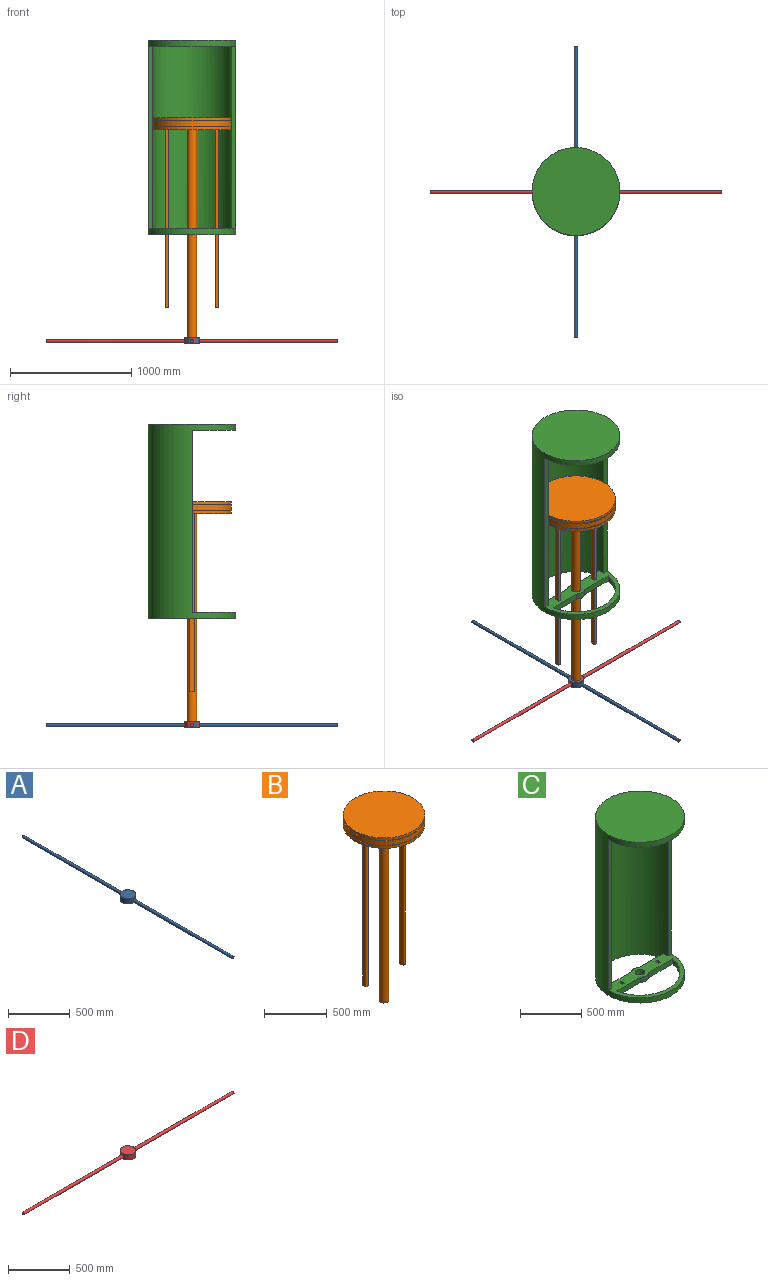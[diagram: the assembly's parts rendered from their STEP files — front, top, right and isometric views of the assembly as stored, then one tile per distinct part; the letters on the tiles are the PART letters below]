
ASSEMBLY  parts=4 mates=3
PART A: 7 faces, bbox 127x2400x50.8 mm
  f0: cylinder r=63.5mm len=127mm, axis (0,0,1), area 19254.8mm2, adj f1,f2,f4,f5
  f1: plane 127x127mm, normal (0,0,-1), area 12667.7mm2, adj f0
  f2: plane 127x127mm, normal (0,0,1), area 12667.7mm2, adj f0
  f3: plane 25.4x25.4mm, normal (0,1,0), area 506.7mm2, adj f4
  f4: cylinder r=12.7mm len=1137.78mm, axis (0,1,0), area 90739.8mm2, adj f0,f3
  f5: cylinder r=12.7mm len=1137.78mm, axis (0,1,0), area 90739.7mm2, adj f0,f6
  f6: plane 25.4x25.4mm, normal (0,-1,0), area 506.7mm2, adj f5
PART B: 25 faces, bbox 648.8x648.8x1813.5 mm
  f0: cylinder r=324.42mm len=648.84mm, axis (0,0,-1), area 48539.4mm2, adj f1,f6
  f1: plane 648.84x648.84mm, normal (0,0,-1), area 142883.7mm2, adj f0,f2
  f2: cylinder r=244.47mm len=488.95mm, axis (0,0,-1), area 58524.7mm2, adj f1,f3
  f3: plane 488.95x488.95mm, normal (0,0,-1), area 181270.9mm2, adj f2,f13,f15,f16,f17,f18,f20,f21
  f4: plane 648.84x648.84mm, normal (0,0,-1), area 6440.3mm2, adj f5,f7
  f5: cylinder r=321.25mm len=642.49mm, axis (0,0,1), area 6408.6mm2, adj f4,f6
  f6: plane 648.84x648.84mm, normal (0,0,1), area 6440.3mm2, adj f0,f5
  f7: cylinder r=324.42mm len=648.84mm, axis (0,0,-1), area 97078.8mm2, adj f4,f10
  f8: plane 648.84x648.84mm, normal (0,0,-1), area 6440.3mm2, adj f9,f12
  f9: cylinder r=321.25mm len=642.49mm, axis (0,0,1), area 6408.6mm2, adj f8,f10
  f10: plane 648.84x648.84mm, normal (0,0,1), area 6440.3mm2, adj f7,f9
  f11: plane 648.84x648.84mm, normal (0,0,1), area 330650.5mm2, adj f12
  f12: cylinder r=324.42mm len=648.84mm, axis (0,0,-1), area 48539.4mm2, adj f8,f11
  f13: cylinder r=38.1mm len=1750mm, axis (0,0,1), area 418931.4mm2, adj f3,f14
  f14: plane 76.2x76.2mm, normal (0,0,-1), area 4560.4mm2, adj f13
  f15: plane 1500x25.4mm, normal (0,-1,0), area 38100mm2, adj f3,f16,f18,f19
  f16: plane 1500x38.1mm, normal (-1,0,0), area 57150mm2, adj f3,f15,f17,f19
  f17: plane 1500x25.4mm, normal (0,1,0), area 38100mm2, adj f3,f16,f18,f19
  f18: plane 1500x38.1mm, normal (1,0,0), area 57150mm2, adj f3,f15,f17,f19
  f19: plane 38.1x25.4mm, normal (0,0,-1), area 967.7mm2, adj f15,f16,f17,f18
  f20: plane 1500x38.1mm, normal (1,0,0), area 57150mm2, adj f3,f21,f23,f24
  f21: plane 1500x25.4mm, normal (0,-1,0), area 38100mm2, adj f3,f20,f22,f24
  f22: plane 1500x38.1mm, normal (-1,0,0), area 57150mm2, adj f3,f21,f23,f24
  f23: plane 1500x25.4mm, normal (0,1,0), area 38100mm2, adj f3,f20,f22,f24
  f24: plane 38.1x25.4mm, normal (0,0,-1), area 967.7mm2, adj f20,f21,f22,f23
PART C: 24 faces, bbox 723.9x723.9x1601.6 mm
  f0: plane 723.9x431.8mm, normal (0,0,1), area 105607.8mm2, adj f1,f2,f3,f4,f5,f6,f7,f8
  f1: plane 275.56x50.8mm, normal (0,-1,0), area 13998.6mm2, adj f0,f2,f18,f19
  f2: cylinder r=69.85mm len=88.67mm, axis (0,0,-1), area 4880.2mm2, adj f0,f1,f3,f19
  f3: plane 275.56x50.8mm, normal (0,-1,0), area 13998.6mm2, adj f0,f2,f18,f19
  f4: cylinder r=324.42mm len=1550.8mm, axis (0,0,-1), area 1575066.2mm2, adj f0,f5,f13,f19,f20,f21,f22
  f5: plane 275.56x50.8mm, normal (0,1,0), area 13998.6mm2, adj f0,f4,f6,f19
  f6: cylinder r=69.85mm len=88.67mm, axis (0,0,-1), area 4880.2mm2, adj f0,f5,f13,f19
  f7: plane 50.8x25.4mm, normal (0,-1,0), area 1290.3mm2, adj f0,f8,f14,f19
  f8: plane 50.8x38.1mm, normal (-1,0,0), area 1935.5mm2, adj f0,f7,f9,f19
  f9: plane 50.8x25.4mm, normal (0,1,0), area 1290.3mm2, adj f0,f8,f14,f19
  f10: plane 50.8x38.1mm, normal (1,0,0), area 1935.5mm2, adj f0,f11,f17,f19
  f11: plane 50.8x25.4mm, normal (0,-1,0), area 1290.3mm2, adj f0,f10,f12,f19
  f12: plane 50.8x38.1mm, normal (-1,0,0), area 1935.5mm2, adj f0,f11,f17,f19
  f13: plane 275.56x50.8mm, normal (0,1,0), area 13998.6mm2, adj f0,f4,f6,f19
  f14: plane 50.8x38.1mm, normal (1,0,0), area 1935.5mm2, adj f0,f7,f9,f19
  f15: cylinder r=361.95mm len=1601.6mm, axis (0,0,-1), area 1936707.8mm2, adj f0,f19,f20,f21,f22,f23
  f16: cylinder r=38.1mm len=76.2mm, axis (0,0,-1), area 12161mm2, adj f0,f19
  f17: plane 50.8x25.4mm, normal (0,1,0), area 1290.3mm2, adj f0,f10,f12,f19
  f18: cylinder r=324.42mm len=639.8mm, axis (0,0,-1), area 46265.9mm2, adj f0,f1,f3,f19
  f19: plane 723.9x723.9mm, normal (0,0,-1), area 146069.2mm2, adj f1,f2,f3,f4,f5,f6,f7,f8
  f20: plane 1500x37.53mm, normal (0,-1,0), area 56292.8mm2, adj f0,f4,f15,f22
  f21: plane 1500x37.53mm, normal (0,-1,0), area 56292.8mm2, adj f0,f4,f15,f22
  f22: plane 723.9x686.37mm, normal (0,0,-1), area 371111.8mm2, adj f4,f15,f20,f21
  f23: plane 723.9x723.9mm, normal (0,0,1), area 411573.1mm2, adj f15
PART D: 7 faces, bbox 2400x127x50.8 mm
  f0: cylinder r=63.5mm len=127mm, axis (0,0,1), area 19254.8mm2, adj f1,f2,f4,f5
  f1: plane 127x127mm, normal (0,0,-1), area 12667.7mm2, adj f0
  f2: plane 127x127mm, normal (0,0,1), area 12667.7mm2, adj f0
  f3: plane 25.4x25.4mm, normal (1,0,0), area 506.7mm2, adj f4
  f4: cylinder r=12.7mm len=1137.78mm, axis (1,0,0), area 90739.8mm2, adj f0,f3
  f5: cylinder r=12.7mm len=1137.78mm, axis (1,0,0), area 90739.7mm2, adj f0,f6
  f6: plane 25.4x25.4mm, normal (-1,0,0), area 506.7mm2, adj f5
PLACE A t=(-51.95,436.29,760.93)mm
PLACE B t=(-51.95,436.29,760.93)mm fixed
PLACE C t=(-51.95,436.29,-101.37)mm
PLACE D t=(-51.95,436.29,760.93)mm
MATE cylindrical B.f13 <-> C.f16  axis (0,0,1) through (-51.95,436.29,-75.97)mm
MATE fastened A.f0 <-> B.f13  axis (0,0,1) through (-51.95,436.29,-950.97)mm
MATE fastened D.f0 <-> A.f0  axis (0,0,1) through (-51.95,436.29,-950.97)mm
